FCSTD DOCUMENT  (FreeCAD 1.0R39109 (Git))
Label: enclosure-dims
License: All rights reserved
LicenseURL: http://en.wikipedia.org/wiki/All_rights_reserved
objects: Spreadsheet::Sheet×1

FEATURE [Spreadsheet::Sheet] Spreadsheet
  cells = A1='floor_t; B1(floor_t)==0.75 in; A2='wall_t; B2(wall_t)==3 mm; A3='fwall_t; B3(fwall_t)==3 mm; A4='lid_t; B4(lid_t)==3 mm; A5='floor_w; B5(floor_w)==38.5 in; A6='floor_d; B6(floor_d)==24 in; A7='lid_w; B7(lid_w)==B5 + 2 * (B2 + B18); A8='lid_d; B8(lid_d)==B6 + 2 * B3; A9='internal_h; B9(vol_h)==12 in; A10='window_w; B10(window_w)==750 mm; A11='window_d; B11(window_d)==460 mm; A12='window_t; B12(window_t)==0.25 in; A13='window_rabbet; B13(window_rabbet)==0.25 in; A14='door_h; B14(door_h)==2.5 in; A15='door_t; B15(door_t)==0.5 in; A16='lid_min_h; B16(lid_min_h)==1 in; A17='exhaust_d; B17(exhaust_d)==24 in; A18='exhaust_w; B18(exhaust_w)==2.25 in; A19='exhaust_d; B19(exhaust_h)==6 in; A20='dragchain_w; B20(draingchain_w)==1 in; A21='base_t; B21(base_t)==0.5 in; A22='base_h; B22(base_h)==36 in; A23='base_w; B23(base_w)==B5 + 2 * B18 + 2 * B21; A24='base_d; B24(base_d)==B6 + 2 * B2; A25='leg_w; B25(leg_w)==3.125 in; A26='leg_t; B26(leg_t)==1.5 in; A27='toekick; B27(toekick)==6 in; A28='frame_w; B28(frame_w)==36.5 in; A29='frame_d; B29(frame_d)==23.75 in; A30='frame_h; B30(frame_h)==8 in; A31='lid_max_h; B31(lid_max_h)==B1 + B9 - (B32 + B14); A32='rail_h; B32(rail_h)==1.25 in; A33='shelf_t; B33(shelf_t)==0.5 in
